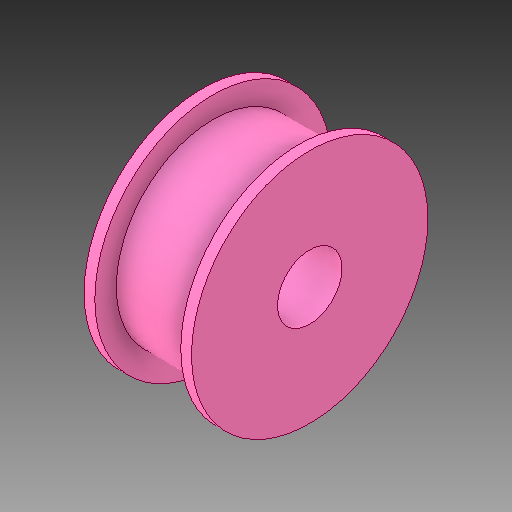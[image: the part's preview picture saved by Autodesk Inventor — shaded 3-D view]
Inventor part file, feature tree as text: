
AUTODESK INVENTOR PART (.ipt)
format: ipt  version: 2017 SP1 (Build 210196100, 196)  size: 141,824 bytes
history: native  units: in
note: dims shown in document units (in); Inventor stores cm internally (conversion verified against a paired STEP export)
features: extrude x4, sketch x4
ambient origin geometry x8: Origin, YZ Plane, XZ Plane, XY Plane, X Axis, Y Axis, Z Axis, Center Point
bodies: Solid1 (feature_tree)
feature tree (8):
  extrude  "Extrusion1"  Depth=0.375in
  extrude  "Extrusion2"  Depth=0.5in
  extrude  "Extrusion3"  Depth=0.0625in TaperAngle=0.0deg
  extrude  "Extrusion4"  Depth=0.1875in TaperAngle=0.0deg
  sketch  "Sketch1"  dims[d0=1.125in d2=0.375in]
  sketch  "Sketch2"  dims[d4=0.5in d5=0.0in d6=0.125in]
  sketch  "Sketch3"  dims[d7=0.0625in d8=0.0in d9=0.0625in d10=0.0in]
  sketch  "Sketch4"  dims[d11=0.1875in d12=0.375in d13=0.0in]
